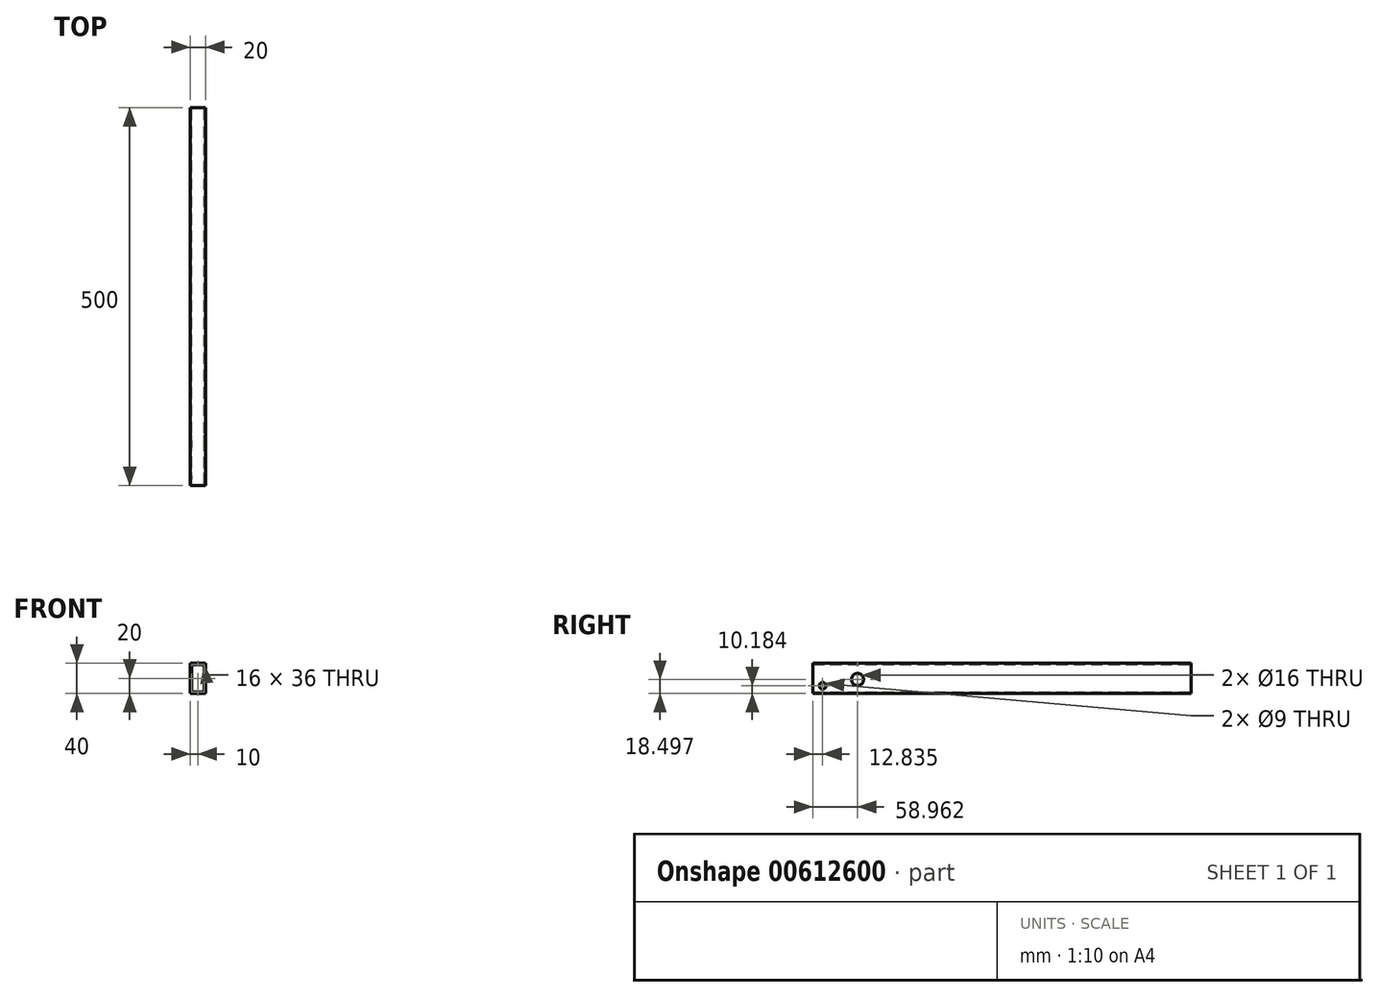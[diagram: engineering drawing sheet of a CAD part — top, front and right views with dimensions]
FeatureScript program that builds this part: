
annotation { "Feature Type Name" : "Feature", "Feature Type Description" : "" }
export const myFeature = defineFeature(function(context is Context, id is Id, definition is map)
    precondition{}
    {
        {
            var Q0;
            Q0=qCreatedBy(makeId("Front.planeOp"),FACE);
            var sketch = newSketch(context, id + "F0", { "sketchPlane" : qUnion([Q0])});
            skLineSegment(sketch, "E0.bottom", {"start": v(0, 0) * mm, "end": v(20, 0) * mm});
            skLineSegment(sketch, "E0.top", {"start": v(0, -40) * mm, "end": v(20, -40) * mm});
            skLineSegment(sketch, "E0.left", {"start": v(0, 0) * mm, "end": v(0, -40) * mm});
            skLineSegment(sketch, "E0.right", {"start": v(20, 0) * mm, "end": v(20, -40) * mm});
            skLineSegment(sketch, "E1.0", {"start": v(2, -2) * mm, "end": v(18, -2) * mm});
            skLineSegment(sketch, "E1.1", {"start": v(2, -2) * mm, "end": v(2, -38) * mm});
            skLineSegment(sketch, "E1.2", {"start": v(2, -38) * mm, "end": v(18, -38) * mm});
            skLineSegment(sketch, "E1.3", {"start": v(18, -2) * mm, "end": v(18, -38) * mm});
            skSolve(sketch);
        }
        {
            var Q0;
            Q0=makeQuery(id+"F0.imprint","IMPRINT",FACE,{"disambiguationData":[TD([[makeQuery(id+"F0.imprint","IMPRINT",EDGE,{"derivedFrom":sQuery(id+"F0.wireOp",EDGE,"E0.bottom")}),-1.0]])]});
            extrude(context, id + "F1", {"entities" : qUnion([Q0]), "depth" : 500 * mm, "offsetDistance" : 25.4 * mm});
        }
        {
            var Q0;
            Q0=makeQuery(id+"F1.opExtrude","SWEPT_FACE",FACE,{"disambiguationData":[OSD([sQuery(id+"F0.wireOp",EDGE,"E0.left")])]});
            var sketch = newSketch(context, id + "F2", { "sketchPlane" : qUnion([Q0])});
            skCircle(sketch, "E2", {"center": v(441.04, -21.5) * mm, "radius": 8 * mm});
            skCircle(sketch, "E3", {"center": v(487.16, -29.82) * mm, "radius": 4.5 * mm});
            skSolve(sketch);
        }
        {
            var Q0;
            Q0=makeQuery(id+"F2.imprint","IMPRINT",FACE,{"disambiguationData":[TD([[makeQuery(id+"F2.imprint","IMPRINT",EDGE,{"derivedFrom":sQuery(id+"F2.wireOp",EDGE,"E3")}),1.0]])]});
            var Q1;
            Q1=makeQuery(id+"F2.imprint","IMPRINT",FACE,{"disambiguationData":[TD([[makeQuery(id+"F2.imprint","IMPRINT",EDGE,{"derivedFrom":sQuery(id+"F2.wireOp",EDGE,"E2")}),1.0]])]});
            extrude(context, id + "F3", {"entities" : qUnion([Q0, Q1]), "operationType" : NewBodyOperationType.REMOVE, "oppositeDirection" : true, "depth" : 25 * mm, "offsetDistance" : 25.4 * mm});
        }
    });
